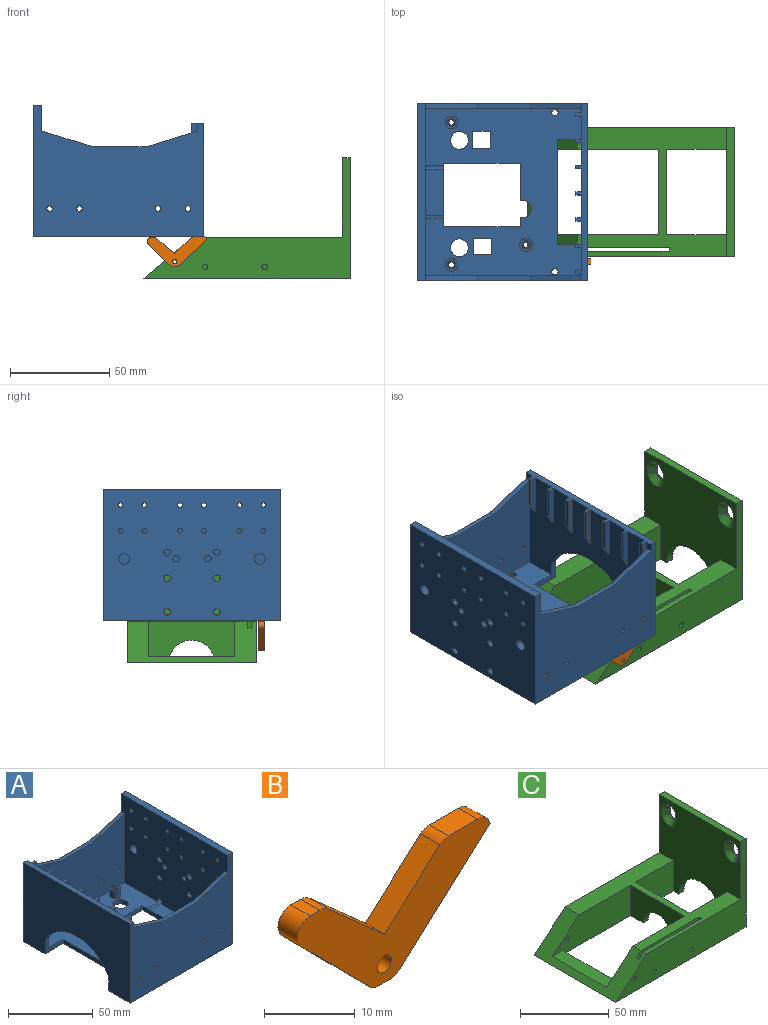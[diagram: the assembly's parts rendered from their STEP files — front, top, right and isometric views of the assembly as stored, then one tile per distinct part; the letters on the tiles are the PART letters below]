
ASSEMBLY  parts=3 mates=1
PART A: 118 faces, bbox 85.5x89x66 mm
  f0: plane 84x78.5mm, normal (0,0,1), area 4050.5mm2, adj f1,f2,f4,f12,f13,f14,f15,f18
  f1: plane 89x54mm, normal (1,0,0), area 3343.4mm2, adj f0,f9,f11,f42,f69,f70,f71,f74
  f2: plane 89x63mm, normal (-1,0,0), area 5196.2mm2, adj f0,f3,f9,f11,f43,f44,f45,f46
  f3: plane 23.04x9mm, normal (0,0,1), area 207.3mm2, adj f2,f18,f44,f58
  f4: plane 4.61x3mm, normal (1,0,0), area 13.8mm2, adj f0,f5,f14,f41
  f5: plane 89x85.5mm, normal (0,0,-1), area 5230.7mm2, adj f4,f9,f10,f11,f12,f13,f14,f15
  f6: plane 3.2x3.2mm, normal (0,0,1), area 1.9mm2, adj f20,f28
  f7: plane 3.2x3.2mm, normal (0,0,1), area 1.9mm2, adj f17,f25
  f8: plane 3.2x3.2mm, normal (0,0,1), area 1.9mm2, adj f19,f22
  f9: plane 85.5x66mm, normal (0,1,0), area 4150.9mm2, adj f1,f2,f5,f10,f16,f42,f43,f71
  f10: plane 89x57mm, normal (-1,0,0), area 3941mm2, adj f5,f9,f11,f42,f103,f104,f105
  f11: plane 85.5x66mm, normal (0,-1,0), area 4150.9mm2, adj f1,f2,f5,f10,f16,f42,f43,f67
  f12: plane 38.52x3mm, normal (0,1,0), area 115.6mm2, adj f0,f5,f13,f18
  f13: plane 18.61x3mm, normal (1,0,0), area 55.8mm2, adj f0,f5,f12,f41
  f14: plane 38.52x3mm, normal (0,-1,0), area 115.6mm2, adj f0,f4,f5,f18
  f15: cylinder r=1.6mm len=3.2mm, axis (0,0,-1), area 30.2mm2, adj f0,f5
  f16: plane 89x66mm, normal (1,0,0), area 5712.3mm2, adj f5,f9,f11,f43,f44,f45,f46,f47
  f17: cylinder r=1.4mm len=3mm, axis (0,0,-1), area 26.4mm2, adj f5,f7
  f18: plane 32x3mm, normal (-1,0,0), area 95.1mm2, adj f0,f3,f5,f12,f14,f44,f58
  f19: cylinder r=1.4mm len=3mm, axis (0,0,-1), area 26.4mm2, adj f5,f8
  f20: cylinder r=1.4mm len=3mm, axis (0,0,-1), area 26.4mm2, adj f5,f6
  f21: cylinder r=1.6mm len=3.2mm, axis (0,0,-1), area 30.2mm2, adj f0,f5
  f22: cylinder r=1.6mm len=4.7mm, axis (0,0,-1), area 47.2mm2, adj f8,f109
  f23: cylinder r=3.25mm len=6.5mm, axis (0,0,-1), area 106.2mm2, adj f0,f24
  f24: plane 6.5x6.5mm, normal (0,0,1), area 19.3mm2, adj f23,f109
  f25: cylinder r=1.6mm len=4.7mm, axis (0,0,-1), area 47.2mm2, adj f7,f108
  f26: cylinder r=3.25mm len=6.5mm, axis (0,0,-1), area 106.2mm2, adj f0,f27
  f27: plane 6.5x6.5mm, normal (0,0,1), area 19.3mm2, adj f26,f108
  f28: cylinder r=1.6mm len=4.7mm, axis (0,0,-1), area 47.2mm2, adj f6,f107
  f29: cylinder r=3.25mm len=6.5mm, axis (0,0,-1), area 106.2mm2, adj f0,f30
  f30: plane 6.5x6.5mm, normal (0,0,1), area 19.3mm2, adj f29,f107
  f31: cylinder r=4.5mm len=9mm, axis (0,0,1), area 84.8mm2, adj f0,f5
  f32: plane 9.18x3mm, normal (0,-1,0), area 27.5mm2, adj f0,f5,f33,f35
  f33: plane 8.06x3mm, normal (1,0,0), area 24.2mm2, adj f0,f5,f32,f34
  f34: plane 9.18x3mm, normal (0,1,0), area 27.5mm2, adj f0,f5,f33,f35
  f35: plane 8.06x3mm, normal (-1,0,0), area 24.2mm2, adj f0,f5,f32,f34
  f36: plane 8.85x3mm, normal (0,-1,0), area 26.5mm2, adj f0,f5,f37,f39
  f37: plane 8.44x3mm, normal (1,0,0), area 25.3mm2, adj f0,f5,f36,f38
  f38: plane 8.85x3mm, normal (0,1,0), area 26.5mm2, adj f0,f5,f37,f39
  f39: plane 8.44x3mm, normal (-1,0,0), area 25.3mm2, adj f0,f5,f36,f38
  f40: cylinder r=4.5mm len=9mm, axis (0,0,1), area 84.8mm2, adj f0,f5
  f41: cylinder r=4.5mm len=9mm, axis (0,0,1), area 48.3mm2, adj f0,f4,f5,f13
  f42: plane 89x6mm, normal (0,0,1), area 301.2mm2, adj f1,f9,f10,f11,f75,f76,f77,f78
  f43: plane 89x4mm, normal (0,0,1), area 356mm2, adj f2,f9,f11,f16
  f44: cylinder r=1.6mm len=13mm, axis (1,0,0), area 59.2mm2, adj f0,f2,f3,f16,f18
  f45: cylinder r=1.15mm len=4mm, axis (1,0,0), area 28.9mm2, adj f2,f16
  f46: cylinder r=1.15mm len=4mm, axis (1,0,0), area 28.9mm2, adj f2,f16
  f47: cylinder r=1.15mm len=4mm, axis (1,0,0), area 28.9mm2, adj f2,f16
  f48: cylinder r=1.15mm len=4mm, axis (1,0,0), area 28.9mm2, adj f2,f16
  f49: cylinder r=1.15mm len=4mm, axis (1,0,0), area 28.9mm2, adj f2,f16
  f50: cylinder r=1.6mm len=4mm, axis (1,0,0), area 40.2mm2, adj f2,f16
  f51: cylinder r=2.75mm len=5.5mm, axis (1,0,0), area 69.1mm2, adj f2,f16
  f52: cylinder r=2.75mm len=5.5mm, axis (1,0,0), area 69.1mm2, adj f2,f16
  f53: cylinder r=1.6mm len=4mm, axis (1,0,0), area 40.2mm2, adj f2,f16
  f54: cylinder r=1.6mm len=4mm, axis (1,0,0), area 40.2mm2, adj f2,f16
  f55: cylinder r=1.6mm len=4mm, axis (1,0,0), area 39mm2, adj f2,f16,f56
  f56: plane 4x0.3mm, normal (0,1,0), area 1.2mm2, adj f2,f16,f55
  f57: cylinder r=1.6mm len=4mm, axis (1,0,0), area 40.2mm2, adj f2,f16
  f58: cylinder r=1.6mm len=13mm, axis (1,0,0), area 59.2mm2, adj f0,f2,f3,f16,f18
  f59: cylinder r=1.15mm len=4mm, axis (1,0,0), area 28.9mm2, adj f2,f16
  f60: cylinder r=1.15mm len=4mm, axis (1,0,0), area 28.9mm2, adj f2,f16
  f61: cylinder r=1.15mm len=4mm, axis (1,0,0), area 28.9mm2, adj f2,f16
  f62: cylinder r=1.15mm len=4mm, axis (1,0,0), area 28.9mm2, adj f2,f16
  f63: cylinder r=1.6mm len=4mm, axis (1,0,0), area 40.2mm2, adj f2,f16
  f64: cylinder r=1.15mm len=4mm, axis (1,0,0), area 28.9mm2, adj f2,f16
  f65: cylinder r=1.15mm len=4mm, axis (1,0,0), area 28.9mm2, adj f2,f16
  f66: cylinder r=1.15mm len=4mm, axis (1,0,0), area 28.9mm2, adj f2,f16
  f67: plane 26x8mm, normal (-0.29,0,0.96), area 68mm2, adj f2,f11,f68,f70
  f68: plane 26.5x2.5mm, normal (0,0,1), area 66.2mm2, adj f11,f67,f69,f70
  f69: plane 26x8mm, normal (0.29,0,0.96), area 68mm2, adj f1,f11,f68,f70
  f70: plane 78.5x50mm, normal (0,1,0), area 3480.4mm2, adj f0,f1,f2,f67,f68,f69,f114,f115
  f71: plane 26x8mm, normal (0.29,0,0.96), area 68mm2, adj f1,f9,f72,f74
  f72: plane 26.5x2.5mm, normal (0,0,1), area 66.2mm2, adj f9,f71,f73,f74
  f73: plane 26x8mm, normal (-0.29,0,0.96), area 68mm2, adj f2,f9,f72,f74
  f74: plane 78.5x50mm, normal (0,-1,0), area 3480.4mm2, adj f0,f1,f2,f71,f72,f73,f110,f111
  f75: plane 21x3mm, normal (0,1,0), area 55.2mm2, adj f1,f42,f77,f96
  f76: plane 21x3mm, normal (0,-1,0), area 55.2mm2, adj f1,f42,f77,f96
  f77: plane 15.8x1.63mm, normal (1,0,0), area 25.8mm2, adj f42,f75,f76,f96
  f78: plane 21x3mm, normal (0,-1,0), area 55.2mm2, adj f1,f42,f79,f97
  f79: plane 15.8x1.63mm, normal (1,0,0), area 25.8mm2, adj f42,f78,f80,f97
  f80: plane 21x3mm, normal (0,1,0), area 55.2mm2, adj f1,f42,f79,f97
  f81: plane 21x3mm, normal (0,-1,0), area 55.2mm2, adj f1,f42,f82,f98
  f82: plane 15.8x1.63mm, normal (1,0,0), area 25.8mm2, adj f42,f81,f83,f98
  f83: plane 21x3mm, normal (0,1,0), area 55.2mm2, adj f1,f42,f82,f98
  f84: plane 21x3mm, normal (0,-1,0), area 55.2mm2, adj f1,f42,f85,f99
  f85: plane 15.8x1.63mm, normal (1,0,0), area 25.8mm2, adj f42,f84,f86,f99
  f86: plane 21x3mm, normal (0,1,0), area 55.2mm2, adj f1,f42,f85,f99
  f87: plane 21x3mm, normal (0,-1,0), area 55.2mm2, adj f1,f42,f88,f100
  f88: plane 15.8x1.63mm, normal (1,0,0), area 25.8mm2, adj f42,f87,f89,f100
  f89: plane 21x3mm, normal (0,1,0), area 55.2mm2, adj f1,f42,f88,f100
  f90: plane 21x3mm, normal (0,-1,0), area 55.2mm2, adj f1,f42,f91,f101
  f91: plane 15.8x1.63mm, normal (1,0,0), area 25.8mm2, adj f42,f90,f92,f101
  f92: plane 21x3mm, normal (0,1,0), area 55.2mm2, adj f1,f42,f91,f101
  f93: plane 21x3mm, normal (0,-1,0), area 55.2mm2, adj f1,f42,f94,f102
  f94: plane 15.8x1.63mm, normal (1,0,0), area 25.8mm2, adj f42,f93,f95,f102
  f95: plane 21x3mm, normal (0,1,0), area 55.2mm2, adj f1,f42,f94,f102
  f96: plane 5.2x3mm, normal (0.87,0,-0.5), area 9.8mm2, adj f1,f75,f76,f77
  f97: plane 5.2x3mm, normal (0.87,0,-0.5), area 9.8mm2, adj f1,f78,f79,f80
  f98: plane 5.2x3mm, normal (0.87,0,-0.5), area 9.8mm2, adj f1,f81,f82,f83
  f99: plane 5.2x3mm, normal (0.87,0,-0.5), area 9.8mm2, adj f1,f84,f85,f86
  f100: plane 5.2x3mm, normal (0.87,0,-0.5), area 9.8mm2, adj f1,f87,f88,f89
  f101: plane 5.2x3mm, normal (0.87,0,-0.5), area 9.8mm2, adj f1,f90,f91,f92
  f102: plane 5.2x3mm, normal (0.87,0,-0.5), area 9.8mm2, adj f1,f93,f94,f95
  f103: plane 15x10mm, normal (0,-1,0), area 66mm2, adj f0,f1,f5,f10,f105,f106
  f104: plane 15x10mm, normal (0,1,0), area 66mm2, adj f0,f1,f5,f10,f105,f106
  f105: cylinder r=30mm len=53mm, axis (-1,0,0), area 194.9mm2, adj f1,f10,f103,f104
  f106: plane 53x3mm, normal (-1,0,0), area 159mm2, adj f0,f5,f103,f104
  f107: cone r=1.6mm half-angle=45deg, axis (0,0,1), area 8.2mm2, adj f28,f30
  f108: cone r=1.6mm half-angle=45deg, axis (0,0,1), area 8.2mm2, adj f25,f27
  f109: cone r=1.6mm half-angle=45deg, axis (0,0,1), area 8.2mm2, adj f22,f24
  f110: cylinder r=1.4mm len=2.8mm, axis (0,-1,0), area 22mm2, adj f9,f74
  f111: cylinder r=1.4mm len=2.8mm, axis (0,-1,0), area 22mm2, adj f9,f74
  f112: cylinder r=1.4mm len=2.8mm, axis (0,-1,0), area 22mm2, adj f9,f74
  f113: cylinder r=1.4mm len=2.8mm, axis (0,-1,0), area 22mm2, adj f9,f74
  f114: cylinder r=1.4mm len=2.8mm, axis (0,-1,0), area 22mm2, adj f11,f70
  f115: cylinder r=1.4mm len=2.8mm, axis (0,-1,0), area 22mm2, adj f11,f70
  f116: cylinder r=1.4mm len=2.8mm, axis (0,-1,0), area 22mm2, adj f11,f70
  f117: cylinder r=1.4mm len=2.8mm, axis (0,-1,0), area 22mm2, adj f11,f70
PART B: 16 faces, bbox 30.1x3x14.8 mm
  f0: plane 8.65x7.77mm, normal (-0.67,0,0.74), area 34.9mm2, adj f1,f8,f9,f15
  f1: plane 8.74x7.78mm, normal (0.66,0,0.75), area 35.1mm2, adj f0,f8,f9,f10
  f2: plane 3x1.51mm, normal (0,0,1), area 4.5mm2, adj f8,f9,f10,f11
  f3: plane 10.79x10.67mm, normal (-0.71,0,-0.7), area 45.5mm2, adj f8,f9,f11,f12
  f4: plane 3x1.85mm, normal (0,0,-1), area 5.6mm2, adj f8,f9,f12,f13
  f5: plane 14.2x12.76mm, normal (0.67,0,-0.74), area 57.3mm2, adj f8,f9,f13,f14
  f6: plane 4.55x3mm, normal (0,0,1), area 13.7mm2, adj f8,f9,f14,f15
  f7: cylinder r=1.1mm len=3mm, axis (0,1,0), area 20.7mm2, adj f8,f9
  f8: plane 30.06x14.79mm, normal (0,-1,0), area 193.1mm2, adj f0,f1,f2,f3,f4,f5,f6,f7
  f9: plane 30.06x14.79mm, normal (0,1,0), area 193.1mm2, adj f0,f1,f2,f3,f4,f5,f6,f7
  f10: cylinder r=2mm len=3mm, axis (0,1,0), area 4.4mm2, adj f1,f2,f8,f9
  f11: cylinder r=2mm len=3.41mm, axis (0,1,0), area 14.1mm2, adj f2,f3,f8,f9
  f12: cylinder r=2mm len=3mm, axis (0,1,0), area 4.7mm2, adj f3,f4,f8,f9
  f13: cylinder r=2mm len=3mm, axis (0,1,0), area 4.4mm2, adj f4,f5,f8,f9
  f14: cylinder r=2mm len=3mm, axis (0,1,0), area 7.9mm2, adj f5,f6,f8,f9
  f15: cylinder r=2mm len=3mm, axis (0,1,0), area 4.4mm2, adj f0,f6,f8,f9
PART C: 44 faces, bbox 104x65x61 mm
  f0: plane 104x65mm, normal (0,0,-1), area 2811.6mm2, adj f4,f5,f7,f8,f10,f12,f13,f14
  f1: plane 75x65mm, normal (0,0,1), area 1729.6mm2, adj f4,f7,f10,f12,f13,f14,f15,f16
  f2: cylinder r=1.4mm len=2.8mm, axis (0,-1,0), area 23.5mm2, adj f12,f42
  f3: cylinder r=1.4mm len=2.8mm, axis (0,-1,0), area 23.5mm2, adj f12,f42
  f4: plane 43x21mm, normal (1,0,0), area 696.3mm2, adj f0,f1,f17,f18,f39
  f5: plane 43x3mm, normal (1,0,0), area 129mm2, adj f0,f14,f15,f38
  f6: cylinder r=1mm len=11mm, axis (0,1,0), area 69.1mm2, adj f12,f14
  f7: plane 65x25mm, normal (-0.64,0,0.77), area 908.9mm2, adj f0,f1,f12,f13,f14,f15,f38,f40
  f8: plane 65x61mm, normal (1,0,0), area 3439.6mm2, adj f0,f9,f12,f13,f19,f20,f21,f22
  f9: plane 65x4mm, normal (0,0,1), area 260mm2, adj f8,f10,f12,f13
  f10: plane 65x61mm, normal (-1,0,0), area 2788.9mm2, adj f0,f1,f9,f12,f13,f17,f18,f27
  f11: cylinder r=1mm len=11mm, axis (0,1,0), area 69.1mm2, adj f13,f15
  f12: plane 104x61mm, normal (0,-1,0), area 2066mm2, adj f0,f1,f2,f3,f6,f7,f8,f9
  f13: plane 104x61mm, normal (0,1,0), area 2078.4mm2, adj f0,f1,f7,f8,f9,f10,f11
  f14: plane 62.43x21mm, normal (0,1,0), area 1078mm2, adj f0,f1,f5,f6,f7,f16,f28,f29
  f15: plane 62.43x21mm, normal (0,-1,0), area 1090.3mm2, adj f0,f1,f5,f7,f11,f16,f38
  f16: plane 43x21mm, normal (-1,0,0), area 696.3mm2, adj f0,f1,f14,f15,f39
  f17: plane 30x21mm, normal (0,-1,0), area 630mm2, adj f0,f1,f4,f10
  f18: plane 30x21mm, normal (0,1,0), area 630mm2, adj f0,f1,f4,f10
  f19: cylinder r=2.55mm len=5.1mm, axis (-1,0,0), area 8mm2, adj f8,f20,f22,f31
  f20: plane 3x1mm, normal (0,-1,0), area 3mm2, adj f8,f19,f21,f33
  f21: cylinder r=2.55mm len=5.1mm, axis (-1,0,0), area 8mm2, adj f8,f20,f22,f32
  f22: plane 3x1mm, normal (0,1,0), area 3mm2, adj f8,f19,f21,f30
  f23: cylinder r=2.55mm len=5.1mm, axis (-1,0,0), area 8mm2, adj f8,f24,f26,f35
  f24: plane 3x1mm, normal (0,-1,0), area 3mm2, adj f8,f23,f25,f37
  f25: cylinder r=2.55mm len=5.1mm, axis (-1,0,0), area 8mm2, adj f8,f24,f26,f36
  f26: plane 3x1mm, normal (0,1,0), area 3mm2, adj f8,f23,f25,f34
  f27: cylinder r=17mm len=34mm, axis (-1,0,0), area 213.6mm2, adj f0,f8,f10
  f28: cylinder r=1.4mm len=6.32mm, axis (0,-1,0), area 55.6mm2, adj f14,f41
  f29: cylinder r=1.4mm len=6.32mm, axis (0,-1,0), area 55.6mm2, adj f14,f41
  f30: plane 3x3mm, normal (-0.71,0.71,0), area 12.7mm2, adj f10,f22,f31,f32
  f31: cone r=2.55mm half-angle=45deg, axis (-1,0,0), area 54mm2, adj f10,f19,f30,f33
  f32: cone r=2.55mm half-angle=45deg, axis (-1,0,0), area 54mm2, adj f10,f21,f30,f33
  f33: plane 3x3mm, normal (-0.71,-0.71,0), area 12.7mm2, adj f10,f20,f31,f32
  f34: plane 3x3mm, normal (-0.71,0.71,0), area 12.7mm2, adj f10,f26,f35,f36
  f35: cone r=2.55mm half-angle=45deg, axis (-1,0,0), area 54mm2, adj f10,f23,f34,f37
  f36: cone r=2.55mm half-angle=45deg, axis (-1,0,0), area 54mm2, adj f10,f25,f34,f37
  f37: plane 3x3mm, normal (-0.71,-0.71,0), area 12.7mm2, adj f10,f24,f35,f36
  f38: plane 43x8.23mm, normal (0,0,1), area 353.8mm2, adj f5,f7,f14,f15
  f39: cylinder r=11.47mm len=22.94mm, axis (1,0,0), area 144.2mm2, adj f0,f4,f16
  f40: plane 17.81x2mm, normal (1,0,0), area 35.6mm2, adj f0,f7,f41,f42
  f41: plane 50x21mm, normal (0,-1,0), area 1031.6mm2, adj f0,f1,f7,f28,f29,f40,f43
  f42: plane 50x21mm, normal (0,1,0), area 1031.6mm2, adj f0,f1,f2,f3,f7,f40,f43
  f43: plane 21x2mm, normal (-1,0,0), area 42mm2, adj f0,f1,f41,f42
PLACE A rot(axis=(0,0,-1),180deg) t=(-163.02,-39.46,13.9)mm
PLACE B rot(axis=(0,-1,0),1.1deg) t=(-45.71,-6.33,-5.89)mm
PLACE C t=(-45.86,-6.33,-7.45)mm fixed
MATE revolute C.f6 <-> B.f7  axis (0,-1,0) through (-130.18,-71.33,1.27)mm
